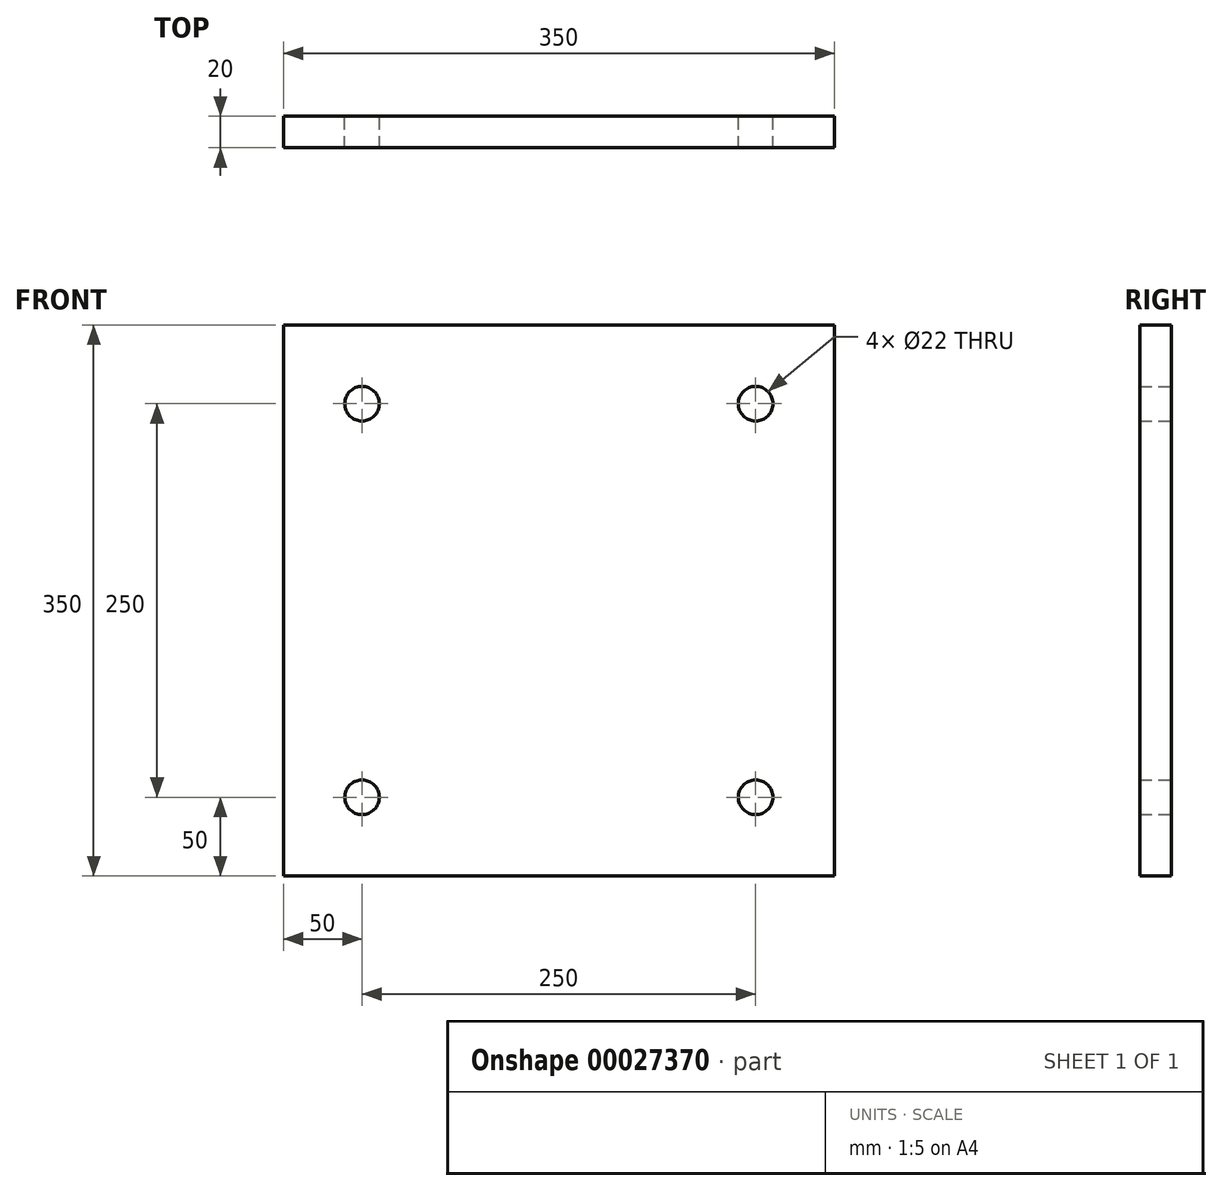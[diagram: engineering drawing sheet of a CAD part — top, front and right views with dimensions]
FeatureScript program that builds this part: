
annotation { "Feature Type Name" : "Feature", "Feature Type Description" : "" }
export const myFeature = defineFeature(function(context is Context, id is Id, definition is map)
    precondition{}
    {
        {
            var Q0;
            Q0=qCreatedBy(makeId("Front.planeOp"),FACE);
            var sketch = newSketch(context, id + "F0", { "sketchPlane" : qUnion([Q0])});
            skLineSegment(sketch, "E0.bottom", {"start": v(0, 0) * mm, "end": v(350, 0) * mm});
            skLineSegment(sketch, "E0.top", {"start": v(0, 350) * mm, "end": v(350, 350) * mm});
            skLineSegment(sketch, "E0.left", {"start": v(0, 0) * mm, "end": v(0, 350) * mm});
            skLineSegment(sketch, "E0.right", {"start": v(350, 0) * mm, "end": v(350, 350) * mm});
            skCircle(sketch, "E1", {"center": v(50, 300) * mm, "radius": 11 * mm});
            skCircle(sketch, "E2", {"center": v(300, 300) * mm, "radius": 11 * mm});
            skCircle(sketch, "E3", {"center": v(300, 50) * mm, "radius": 11 * mm});
            skCircle(sketch, "E4", {"center": v(50, 50) * mm, "radius": 11 * mm});
            skSolve(sketch);
        }
        {
            var Q0;
            Q0=makeQuery(id+"F0.imprint","IMPRINT",FACE,{"disambiguationData":[TD([[makeQuery(id+"F0.imprint","IMPRINT",EDGE,{"derivedFrom":sQuery(id+"F0.wireOp",EDGE,"E0.bottom")}),1.0]])]});
            extrude(context, id + "F1", {"entities" : qUnion([Q0]), "depth" : 20 * mm});
        }
    });
